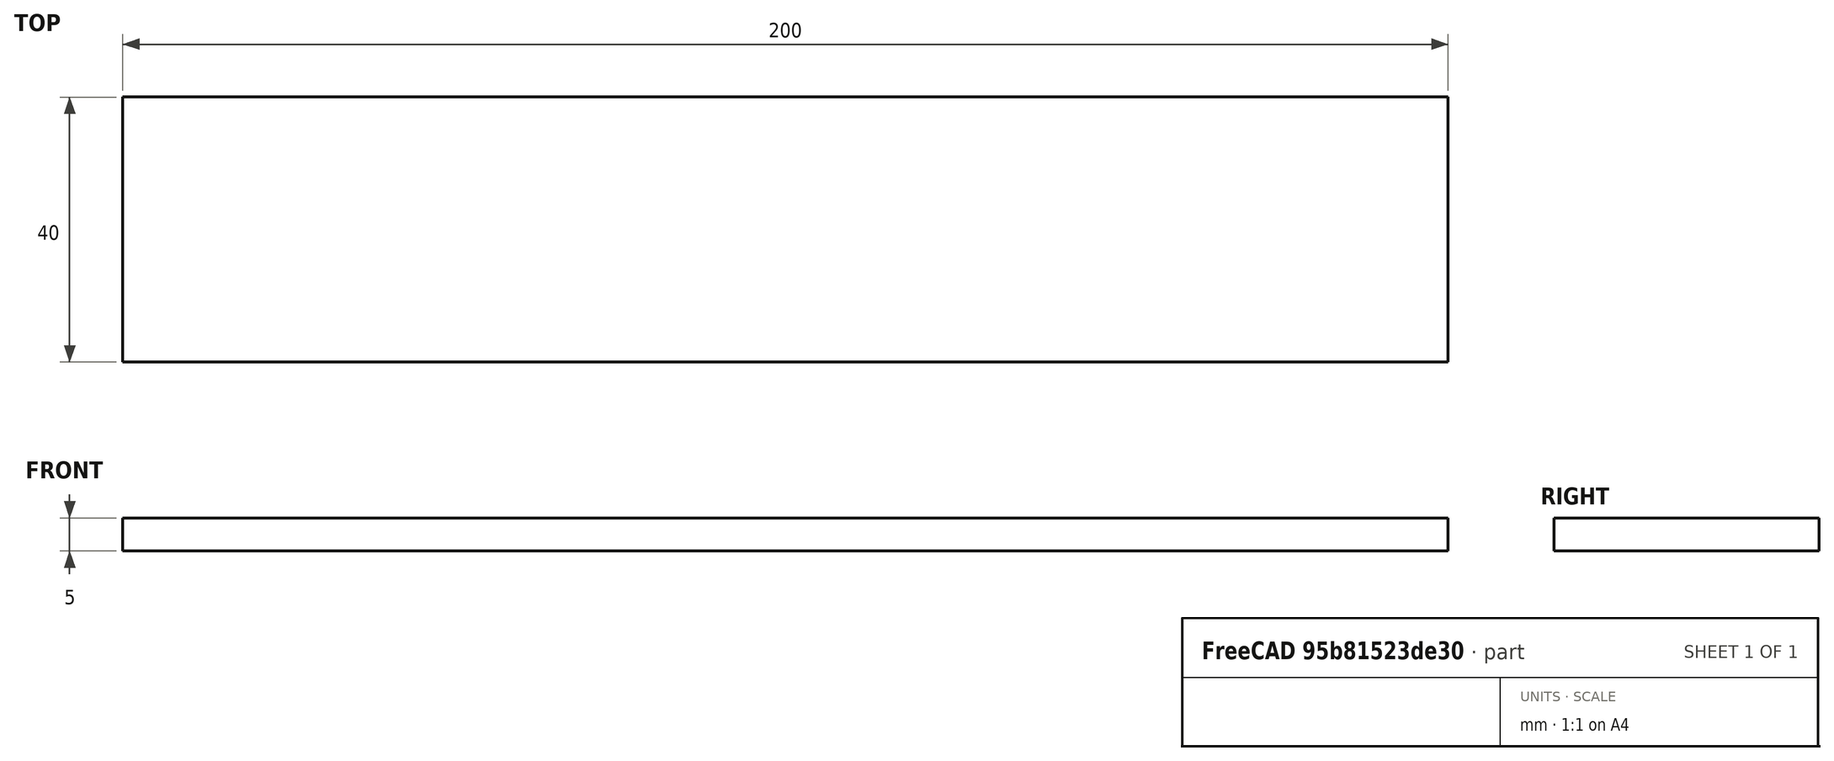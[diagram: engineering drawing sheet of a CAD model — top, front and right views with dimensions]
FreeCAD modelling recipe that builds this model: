
FCSTD DOCUMENT  (FreeCAD 0.17R13541 (Git))
Label: 200x40x5rectangle
License: All rights reserved
LicenseURL: http://en.wikipedia.org/wiki/All_rights_reserved
objects: Sketcher::SketchObject×1, Part::Extrusion×1
note: 2 computed .brp shape members not serialized (recipe doc carries the construction recipe); baked Part::Feature solids carry a one-line shape summary decoded from their .brp

FEATURE [Sketcher::SketchObject] Sketch
  sketch-geometry (4):
    g0: LineSegment StartX=-102.11 StartY=19.1732 StartZ=0 EndX=97.89 EndY=19.1732 EndZ=0
    g1: LineSegment StartX=97.89 StartY=19.1732 StartZ=0 EndX=97.89 EndY=-20.8268 EndZ=0
    g2: LineSegment StartX=97.89 StartY=-20.8268 StartZ=0 EndX=-102.11 EndY=-20.8268 EndZ=0
    g3: LineSegment StartX=-102.11 StartY=-20.8268 StartZ=0 EndX=-102.11 EndY=19.1732 EndZ=0
  constraints (12):
    c: Coincident(g0,g1)
    c: Coincident(g1,g2)
    c: Coincident(g2,g3)
    c: Coincident(g3,g0)
    c: Horizontal(g0)
    c: Horizontal(g2)
    c: Vertical(g1)
    c: Vertical(g3)
    c: Equal(g2,g0)
    c: Distance(g0) = 200
    c: Equal(g1,g3)
    c: Distance(g1) = 40
FEATURE [Part::Extrusion] Extrude
  Base = -> Sketch
  Dir = (0,0,1)
  DirMode = 2
  FaceMakerClass = Part::FaceMakerBullseye
  LengthFwd = 5
  LengthRev = 0
  Solid = true
  Symmetric = false
